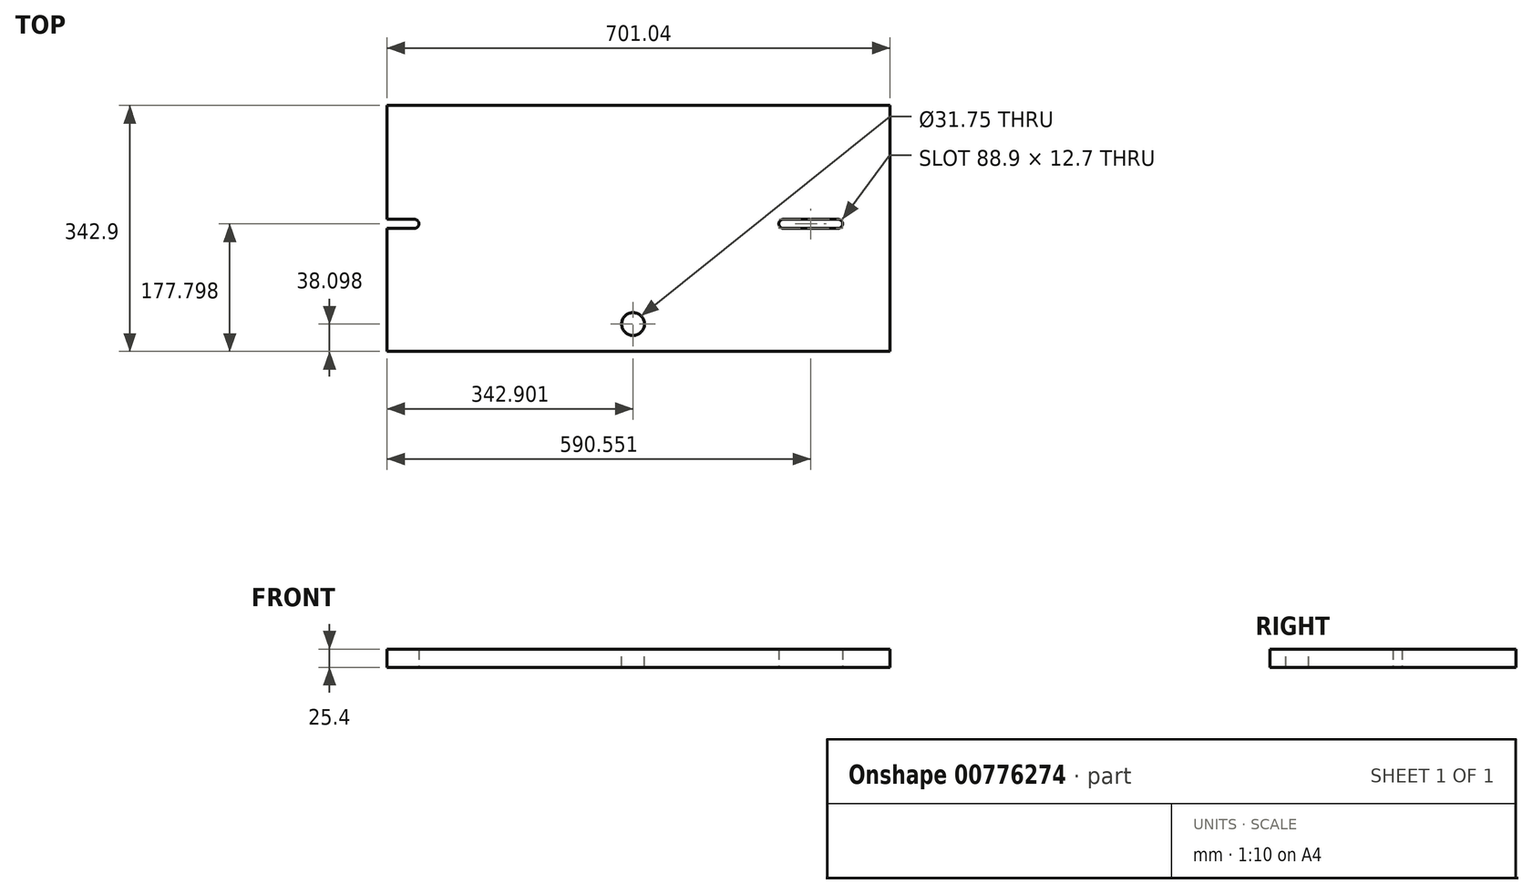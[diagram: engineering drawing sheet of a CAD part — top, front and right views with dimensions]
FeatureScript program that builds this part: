
annotation { "Feature Type Name" : "Feature", "Feature Type Description" : "" }
export const myFeature = defineFeature(function(context is Context, id is Id, definition is map)
    precondition{}
    {
        {
            var Q0;
            Q0=qCreatedBy(makeId("Top.planeOp"),FACE);
            var sketch = newSketch(context, id + "F0", { "sketchPlane" : qUnion([Q0])});
            skLineSegment(sketch, "E0.bottom", {"start": v(-347.54, 182.44) * mm, "end": v(353.5, 182.44) * mm});
            skLineSegment(sketch, "E0.top", {"start": v(-347.54, -160.46) * mm, "end": v(353.5, -160.46) * mm});
            skLineSegment(sketch, "E0.left", {"start": v(-347.54, 182.44) * mm, "end": v(-347.54, 23.69) * mm});
            skLineSegment(sketch, "E0.right", {"start": v(353.5, 182.44) * mm, "end": v(353.5, -160.46) * mm});
            skArc(sketch, "E1", {"start": v(-309.46, 10.99) * mm, "mid": v(-303.09, 17.33) * mm, "end": v(-309.44, 23.69) * mm});
            skArc(sketch, "E2", {"start": v(204.91, 23.69) * mm, "mid": v(198.56, 17.34) * mm, "end": v(204.91, 10.99) * mm});
            skArc(sketch, "E3", {"start": v(281.11, 10.99) * mm, "mid": v(287.46, 17.34) * mm, "end": v(281.11, 23.69) * mm});
            skLineSegment(sketch, "E4", {"start": v(-309.42, 10.99) * mm, "end": v(-347.54, 10.99) * mm});
            skLineSegment(sketch, "E5", {"start": v(-309.44, 23.69) * mm, "end": v(-347.54, 23.69) * mm});
            skLineSegment(sketch, "E6.trimOffspring", {"start": v(-347.54, 10.99) * mm, "end": v(-347.54, -160.46) * mm});
            skLineSegment(sketch, "E7", {"start": v(204.91, 23.69) * mm, "end": v(281.11, 23.69) * mm});
            skLineSegment(sketch, "E8", {"start": v(204.91, 10.99) * mm, "end": v(281.11, 10.99) * mm});
            skSolve(sketch);
        }
        {
            var Q0;
            Q0 = qSketchRegion(id + "F0", true);
            extrude(context, id + "F1", {"entities" : qUnion([Q0]), "depth" : 25.4 * mm, "offsetDistance" : 25.4 * mm});
        }
        {
            var Q0;
            Q0=makeQuery(id+"F1.opExtrude","CAP_FACE",FACE,{"disambiguationData":[OSD([sQuery(id+"F0.wireOp",EDGE,"E0.bottom"),sQuery(id+"F0.wireOp",EDGE,"E0.top"),sQuery(id+"F0.wireOp",EDGE,"E0.left"),sQuery(id+"F0.wireOp",EDGE,"E0.right"),sQuery(id+"F0.wireOp",EDGE,"E1"),sQuery(id+"F0.wireOp",EDGE,"E2"),sQuery(id+"F0.wireOp",EDGE,"E3"),sQuery(id+"F0.wireOp",EDGE,"E4"),sQuery(id+"F0.wireOp",EDGE,"E5"),sQuery(id+"F0.wireOp",EDGE,"E6.trimOffspring"),sQuery(id+"F0.wireOp",EDGE,"E7"),sQuery(id+"F0.wireOp",EDGE,"E8")])],"isStart":false});
            var sketch = newSketch(context, id + "F2", { "sketchPlane" : qUnion([Q0])});
            skCircle(sketch, "E9", {"center": v(-4.64, -122.36) * mm, "radius": 15.88 * mm});
            skSolve(sketch);
        }
        {
            var Q0;
            Q0 = qSketchRegion(id + "F2", true);
            extrude(context, id + "F3", {"entities" : qUnion([Q0]), "operationType" : NewBodyOperationType.REMOVE, "endBound" : BoundingType.THROUGH_ALL, "oppositeDirection" : true, "depth" : 25.4 * mm, "offsetDistance" : 25.4 * mm});
        }
    });
